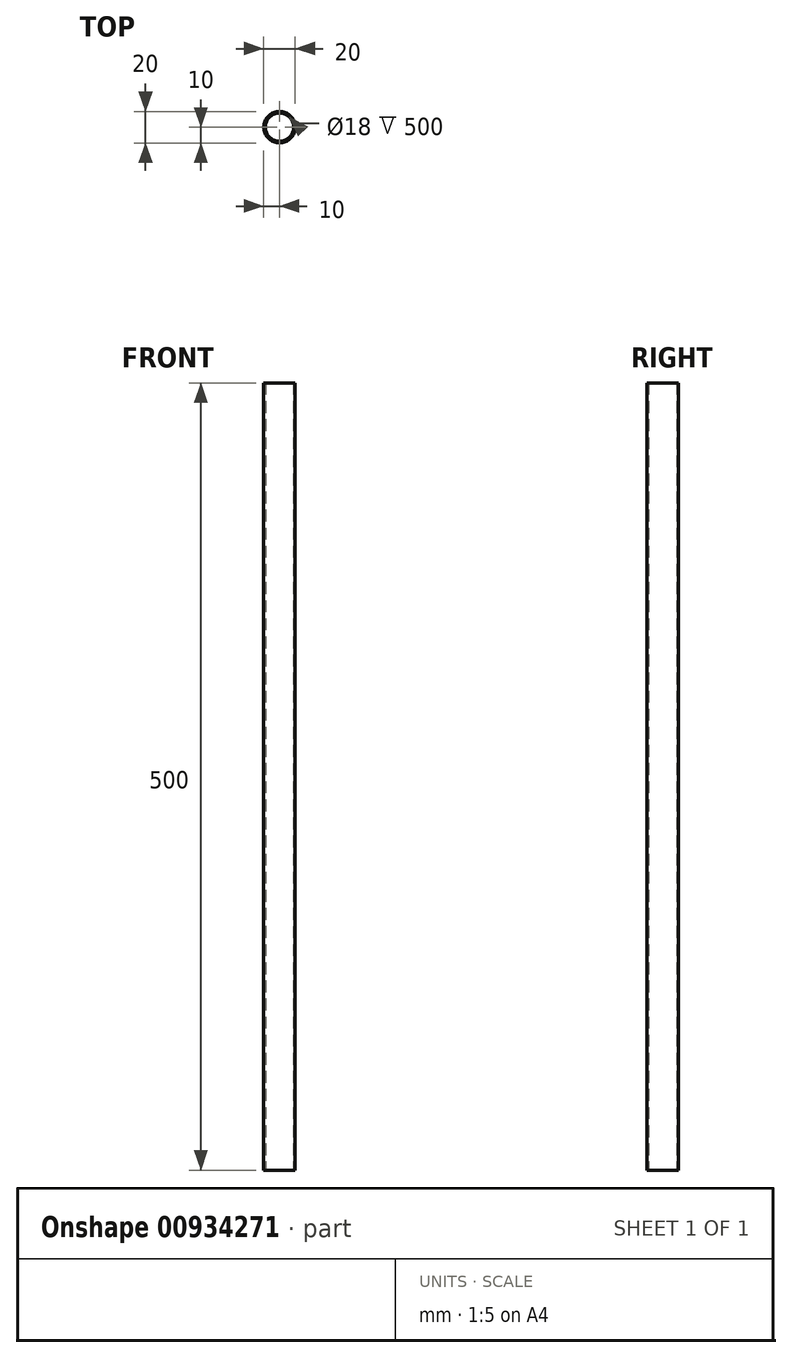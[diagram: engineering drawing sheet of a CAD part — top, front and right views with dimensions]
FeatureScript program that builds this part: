
annotation { "Feature Type Name" : "Feature", "Feature Type Description" : "" }
export const myFeature = defineFeature(function(context is Context, id is Id, definition is map)
    precondition{}
    {
        {
            var Q0;
            Q0=qCreatedBy(makeId("Top.planeOp"),FACE);
            var sketch = newSketch(context, id + "F0", { "sketchPlane" : qUnion([Q0])});
            skCircle(sketch, "E0", {"center": v(0, 0) * mm, "radius": 9 * mm});
            skCircle(sketch, "E1", {"center": v(0, 0) * mm, "radius": 10 * mm});
            skSolve(sketch);
        }
        {
            var Q0;
            Q0 = qSketchRegion(id + "F0", true);
            extrude(context, id + "F1", {"entities" : qUnion([Q0]), "depth" : 500 * mm, "offsetDistance" : 25.4 * mm});
        }
    });
